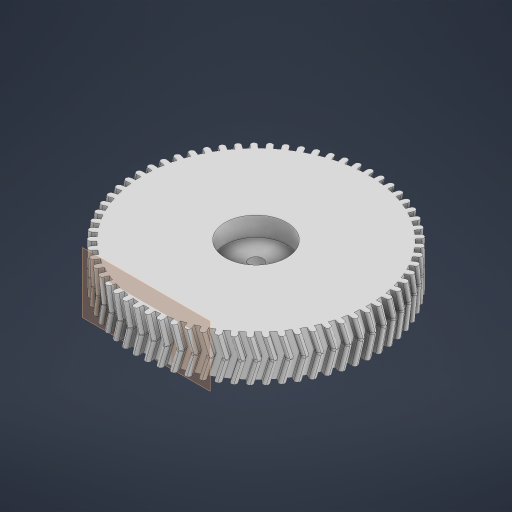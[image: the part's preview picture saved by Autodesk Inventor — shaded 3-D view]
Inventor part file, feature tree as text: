
AUTODESK INVENTOR PART (.ipt)
format: ipt  version: 2023 (Build 270158030, 158C)  size: 1,175,040 bytes
history: native  units: in
note: dims shown in document units (in); Inventor stores cm internally (conversion verified against a paired STEP export)
features: extrude x4, sketch x4, plane x1, fillet x1, pattern_circular x1
ambient origin geometry x8: Origin, YZ Plane, XZ Plane, XY Plane, X Axis, Y Axis, Z Axis, Center Point
bodies: Solid1 (feature_tree)
feature tree (11):
  extrude  "Extrusion1"  Depth=0.5906in TaperAngle=0.0deg
  plane  "Work Plane1"
  extrude  "Extrusion2"  Depth=1.565in
  extrude  "Extrusion3"  Depth=0.0787in
  fillet  "Fillet2"  Radius=0.1378in
  pattern_circular  "Circular Pattern3"  [2 undecoded]
  extrude  "Extrusion9"  Depth=0.2756in TaperAngle=0.0deg
  sketch  "Sketch3"  dims[d0=3.2087in d1=0.5906in d2=0.0in]
  sketch  "Sketch8"  dims[d3=1.565in d4=0.0787in]
  sketch  "Sketch10"  dims[d5=0.0787in d6=0.0787in d7=0.1378in d8=0.0in]
  sketch  "Sketch22"  dims[d17=0.1969in d18=0.1732in d19=2.3622in d20=0.0in d25=0.0394in d26=25.5906in d27=360.0deg d48=0.874in d49=0.2756in d50=0.0in]
note: 2 required parameter values undecoded (feature->parameter linkage not recoverable at this tier; creation-order binding heuristic only, values carry confidence <= 0.55)
